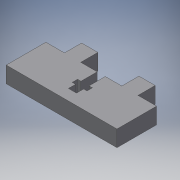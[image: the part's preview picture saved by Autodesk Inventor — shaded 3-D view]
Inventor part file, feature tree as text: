
AUTODESK INVENTOR PART (.ipt)
format: ipt  version: 2019 (Build 230136000, 136)  size: 117,760 bytes
history: native  units: in
note: dims shown in document units (in); Inventor stores cm internally (conversion verified against a paired STEP export)
features: other x2, extrude x1, sketch x1, reference x1, helix x1
ambient origin geometry x8: Origin, YZ Plane, XZ Plane, XY Plane, X Axis, Y Axis, Z Axis, Center Point
bodies: Solid1 (feature_tree)
feature tree (6):
  extrude  "Extrusion1"  [1 undecoded]
  sketch  "Sketch1"  dims[d0=0.2362in d1=0.0in]
  reference  "Reference1"
  other  "<userpath>\Documents\CAD Files\Helix DLP\Helix DLP.iam"
  helix  "Helix DLP.iam"  [1 undecoded]
  other  "rod holder:1"
note: 2 required parameter values undecoded (feature->parameter linkage not recoverable at this tier; creation-order binding heuristic only, values carry confidence <= 0.55)
